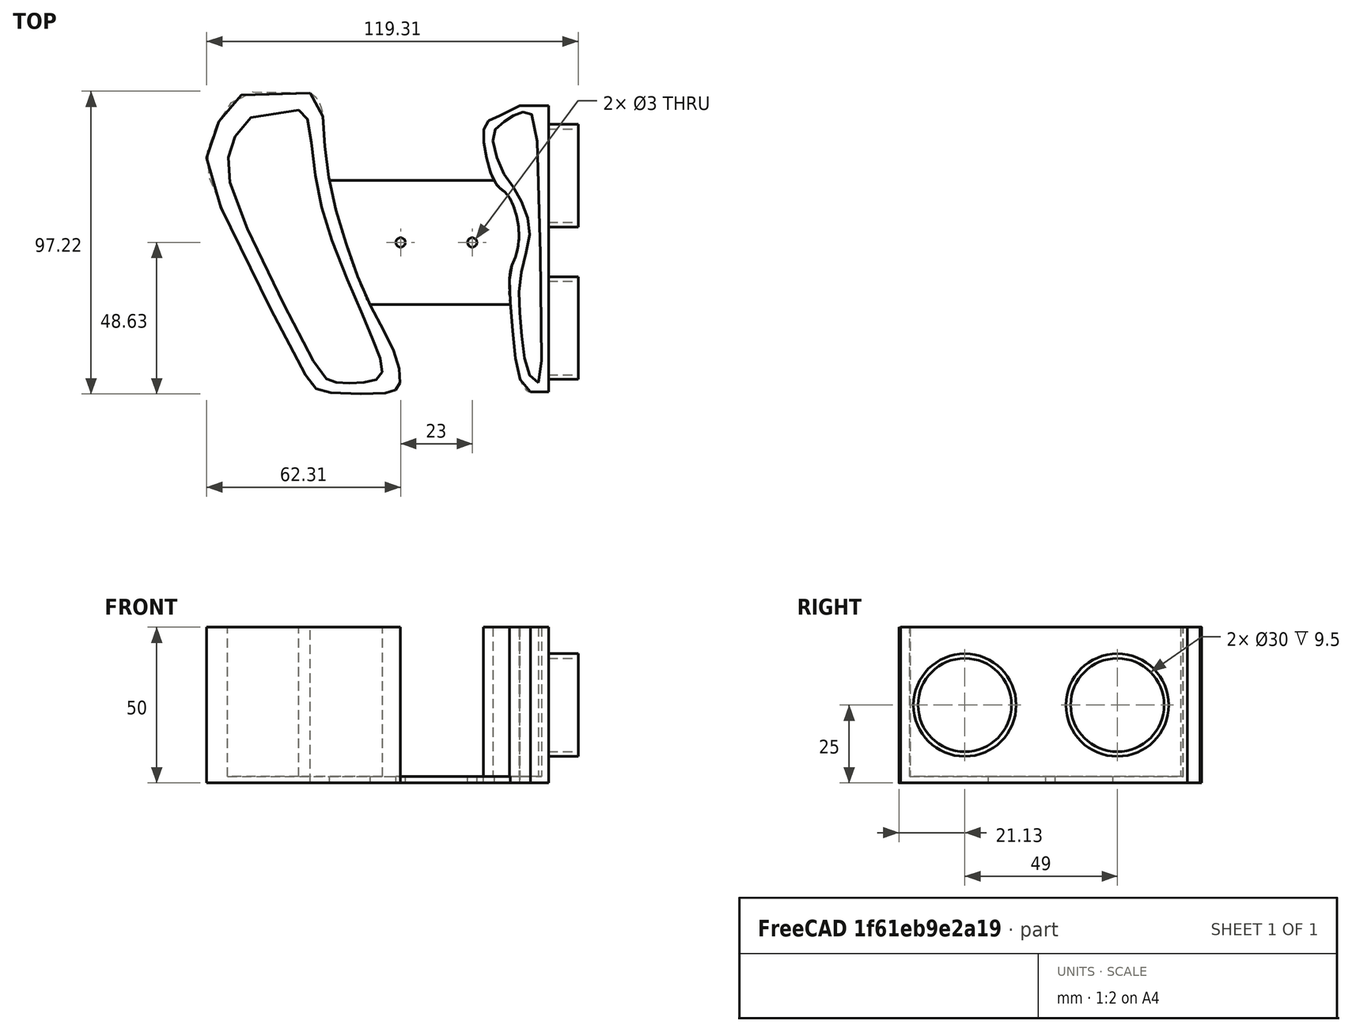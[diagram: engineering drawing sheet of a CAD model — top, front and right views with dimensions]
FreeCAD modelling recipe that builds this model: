
FCSTD DOCUMENT  (FreeCAD 0.18R4 (GitTag))
Label: soporte_pistola_calor
License: All rights reserved
LicenseURL: http://en.wikipedia.org/wiki/All_rights_reserved
objects: Sketcher::SketchObject×8, Part::Cut×6, Part::Cylinder×6, PartDesign::Pad×4, PartDesign::Body×4, Part::MultiFuse×4, Part::Box×3, Image::ImagePlane×1, PartDesign::ShapeBinder×1, App::DocumentObjectGroup×1, Mesh::Feature×1
note: 40 computed .brp shape members not serialized (recipe doc carries the construction recipe); baked Part::Feature solids carry a one-line shape summary decoded from their .brp

FEATURE [Image::ImagePlane] ImagePlane
  XSize = 218.296
  YSize = 300.157
FEATURE [Sketcher::SketchObject] Sketch
  MapMode = 5
  Support = -> [XY_Plane]
  sketch-geometry (39):
    g0-g19: Circle [constr] x20 (B-spline internal-alignment scaffolding for g20; pole/knot coordinates omitted)
    g20: BSplineCurve PolesCount=20 KnotsCount=18 Degree=3 IsPeriodic=0
    g21-g38: GeomPoint [constr] x18 (B-spline internal-alignment scaffolding for g20; pole/knot coordinates omitted)
  constraints (5):
    c: Radius(g0) = 0.7
    c: Equal(g0, g1-g19) x19
    c: Coincident(g19,g0)
    c: InternalAlignment(g0-g19 -> g20) x20
    c: InternalAlignment(g21-g38 -> g20) x18
FEATURE [PartDesign::Pad] Pad
  Length = 50
  Length2 = 100
  Profile = -> Sketch
  Refine = true
  Type = 0
FEATURE [PartDesign::Body] Body
  Group = -> [Sketch,Pad]
  Origin = -> Origin
  Tip = -> Pad
FEATURE [Sketcher::SketchObject] Sketch001
  MapMode = 5
  Support = -> [XY_Plane001]
  sketch-geometry (27):
    g0-g13: Circle [constr] x14 (B-spline internal-alignment scaffolding for g14; pole/knot coordinates omitted)
    g14: BSplineCurve PolesCount=14 KnotsCount=12 Degree=3 IsPeriodic=0
    g15-g26: GeomPoint [constr] x12 (B-spline internal-alignment scaffolding for g14; pole/knot coordinates omitted)
  constraints (5):
    c: Radius(g0) = 1
    c: Equal(g0, g1-g13) x13
    c: Coincident(g13,g0)
    c: InternalAlignment(g0-g13 -> g14) x14
    c: InternalAlignment(g15-g26 -> g14) x12
FEATURE [PartDesign::Pad] Pad001
  Length = 50
  Length2 = 100
  Profile = -> Sketch001
  Refine = true
  Type = 0
FEATURE [Part::Box] Box  label="Cube"
  AttacherType = Attacher::AttachEngine3D
  Height = 50
  Length = 6
  Placement = pos=(21.5,-33.57,0) rot=(0,0,1;0rad)
  Width = 90
FEATURE [Part::Box] Box001  label="Cube001"
  AttacherType = Attacher::AttachEngine3D
  Height = 50
  Length = 9.3
  Placement = pos=(18.2,0,0) rot=(0,0,1;0rad)
  Width = 58.5
FEATURE [Part::Box] Box002  label="Cube002"
  AttacherType = Attacher::AttachEngine3D
  Height = 2
  Length = 63
  Placement = pos=(-44,-5.5,0) rot=(0,0,1;0rad)
  Width = 40
FEATURE [Sketcher::SketchObject] Sketch002
  MapMode = 5
  Placement = pos=(0,0,50) rot=(0,0,1;0rad)
  Support = -> [Pad]
FEATURE [PartDesign::ShapeBinder] CopyPad
  Placement = pos=(0,0,50) rot=(0,0,1;0rad)
  TraceSupport = false
FEATURE [Sketcher::SketchObject] Sketch003
  MapMode = 5
  Placement = pos=(0,0,50) rot=(0,0,1;0rad)
  Support = -> [CopyPad]
  sketch-geometry (15):
    g0: Circle [constr] CenterX=-68.4142 CenterY=53.8043 CenterZ=0 NormalX=0 NormalY=0 NormalZ=1 AngleXU=0 Radius=1
    g1: Circle [constr] CenterX=-72.7746 CenterY=48.5095 CenterZ=0 NormalX=0 NormalY=0 NormalZ=1 AngleXU=0 Radius=1
    g2: Circle [constr] CenterX=-75.422 CenterY=38.8543 CenterZ=0 NormalX=0 NormalY=0 NormalZ=1 AngleXU=0 Radius=1
    g3: Circle [constr] CenterX=-69.0371 CenterY=19.0767 CenterZ=0 NormalX=0 NormalY=0 NormalZ=1 AngleXU=0 Radius=1
    g4: Circle [constr] CenterX=-52.6855 CenterY=-15.3396 CenterZ=0 NormalX=0 NormalY=0 NormalZ=1 AngleXU=0 Radius=1
    g5: Circle [constr] CenterX=-43.3418 CenterY=-29.0437 CenterZ=0 NormalX=0 NormalY=0 NormalZ=1 AngleXU=0 Radius=1
    g6: Circle [constr] CenterX=-26.2115 CenterY=-31.224 CenterZ=0 NormalX=0 NormalY=0 NormalZ=1 AngleXU=0 Radius=1
    g7: Circle [constr] CenterX=-24.187 CenterY=-25.9292 CenterZ=0 NormalX=0 NormalY=0 NormalZ=1 AngleXU=0 Radius=1
    g8: Circle [constr] CenterX=-27.1459 CenterY=-17.364 CenterZ=0 NormalX=0 NormalY=0 NormalZ=1 AngleXU=0 Radius=1
    g9: Circle [constr] CenterX=-38.047 CenterY=4.12663 CenterZ=0 NormalX=0 NormalY=0 NormalZ=1 AngleXU=0 Radius=1
    g10: Circle [constr] CenterX=-46.4564 CenterY=27.6418 CenterZ=0 NormalX=0 NormalY=0 NormalZ=1 AngleXU=0 Radius=1
    g11: Circle [constr] CenterX=-49.571 CenterY=47.2637 CenterZ=0 NormalX=0 NormalY=0 NormalZ=1 AngleXU=0 Radius=1
    g12: Circle [constr] CenterX=-50.3496 CenterY=56.6075 CenterZ=0 NormalX=0 NormalY=0 NormalZ=1 AngleXU=0 Radius=1
    g13: Circle [constr] CenterX=-62.9637 CenterY=58.6319 CenterZ=0 NormalX=0 NormalY=0 NormalZ=1 AngleXU=0 Radius=1
    g14: Circle [constr] CenterX=-70.1272 CenterY=57.3861 CenterZ=0 NormalX=0 NormalY=0 NormalZ=1 AngleXU=0 Radius=1
  constraints (2):
    c: Radius(g0) = 1
    c: Equal(g0, g1-g14) x14
FEATURE [PartDesign::Body] Body001
  Group = -> [Sketch001,Pad001,Sketch002,CopyPad,Sketch003]
  Origin = -> Origin001
  Tip = -> Pad001
FEATURE [Part::MultiFuse] Fusion
  Refine = true
  Shapes = -> [Body001,Box]
FEATURE [Part::MultiFuse] Fusion001
  Refine = true
  Shapes = -> [Box001,Fusion]
FEATURE [Sketcher::SketchObject] Sketch004
  MapMode = 5
  Placement = pos=(0,0,50) rot=(0,0,1;0rad)
  Support = -> [Pad]
  sketch-geometry (33):
    g0-g16: Circle [constr] x17 (B-spline internal-alignment scaffolding for g17; pole/knot coordinates omitted)
    g17: BSplineCurve PolesCount=17 KnotsCount=15 Degree=3 IsPeriodic=0
    g18-g32: GeomPoint [constr] x15 (B-spline internal-alignment scaffolding for g17; pole/knot coordinates omitted)
  constraints (5):
    c: Radius(g0) = 2
    c: Equal(g0, g1-g16) x16
    c: Coincident(g16,g0)
    c: InternalAlignment(g0-g16 -> g17) x17
    c: InternalAlignment(g18-g32 -> g17) x15
FEATURE [Sketcher::SketchObject] CopySketch004
  Placement = pos=(0,0,50) rot=(0,0,1;0rad)
  sketch-geometry (33):
    g0-g16: Circle [constr] x17 (B-spline internal-alignment scaffolding for g17; pole/knot coordinates omitted)
    g17: BSplineCurve PolesCount=17 KnotsCount=15 Degree=3 IsPeriodic=0
    g18-g32: GeomPoint [constr] x15 (B-spline internal-alignment scaffolding for g17; pole/knot coordinates omitted)
  constraints (5):
    c: Radius(g0) = 2
    c: Equal(g0, g1-g16) x16
    c: Coincident(g16,g0)
    c: InternalAlignment(g0-g16 -> g17) x17
    c: InternalAlignment(g18-g32 -> g17) x15
FEATURE [PartDesign::Pad] Pad002
  Length = 48
  Length2 = 100
  Placement = pos=(0,0,50) rot=(0,0,1;0rad)
  Profile = -> CopySketch004
  Refine = true
  Type = 0
FEATURE [PartDesign::Body] Body002
  Group = -> [Pad002]
  Origin = -> Origin002
  Placement = pos=(0,0,-48) rot=(0,0,1;0rad)
  Tip = -> Pad002
FEATURE [Part::Cut] Cut
  Base = -> Body
  Refine = true
  Tool = -> Body002
FEATURE [Sketcher::SketchObject] Sketch005
  MapMode = 5
  Placement = pos=(0,0,0) rot=(1,0,0;3.14159rad)
  Support = -> [Fusion001]
  sketch-geometry (39):
    g0-g19: Circle [constr] x20 (B-spline internal-alignment scaffolding for g20; pole/knot coordinates omitted)
    g20: BSplineCurve PolesCount=20 KnotsCount=18 Degree=3 IsPeriodic=0
    g21-g38: GeomPoint [constr] x18 (B-spline internal-alignment scaffolding for g20; pole/knot coordinates omitted)
  constraints (5):
    c: Radius(g0) = 0.2
    c: Equal(g0, g1-g19) x19
    c: Coincident(g19,g0)
    c: InternalAlignment(g0-g19 -> g20) x20
    c: InternalAlignment(g21-g38 -> g20) x18
FEATURE [App::DocumentObjectGroup] Group
  Group = -> [Sketch004,Sketch005]
FEATURE [Sketcher::SketchObject] CopySketch005
  Placement = pos=(0,0,0) rot=(1,0,0;3.14159rad)
  sketch-geometry (39):
    g0-g19: Circle [constr] x20 (B-spline internal-alignment scaffolding for g20; pole/knot coordinates omitted)
    g20: BSplineCurve PolesCount=20 KnotsCount=18 Degree=3 IsPeriodic=0
    g21-g38: GeomPoint [constr] x18 (B-spline internal-alignment scaffolding for g20; pole/knot coordinates omitted)
  constraints (5):
    c: Radius(g0) = 0.2
    c: Equal(g0, g1-g19) x19
    c: Coincident(g19,g0)
    c: InternalAlignment(g0-g19 -> g20) x20
    c: InternalAlignment(g21-g38 -> g20) x18
FEATURE [PartDesign::Pad] Pad003
  Length = 48
  Length2 = 100
  Placement = pos=(0,0,0) rot=(1,0,0;3.14159rad)
  Profile = -> CopySketch005
  Refine = true
  Type = 0
FEATURE [PartDesign::Body] Body003
  Group = -> [Pad003]
  Origin = -> Origin003
  Placement = pos=(0,0,50) rot=(0,0,1;0rad)
  Tip = -> Pad003
FEATURE [Part::Cut] Cut001
  Base = -> Fusion001
  Refine = true
  Tool = -> Body003
FEATURE [Part::MultiFuse] Fusion002
  Refine = true
  Shapes = -> [Box002,Cut,Cut001]
FEATURE [Part::Cylinder] Cylinder
  Angle = 360
  AttacherType = Attacher::AttachEngine3D
  Height = 10
  Placement = pos=(3,14.5,-4) rot=(0,0,1;0rad)
  Radius = 1.5
FEATURE [Part::Cylinder] Cylinder001
  Angle = 360
  AttacherType = Attacher::AttachEngine3D
  Height = 10
  Placement = pos=(-20,14.5,-4) rot=(0,0,1;0rad)
  Radius = 1.5
FEATURE [Part::Cut] Cut002
  Base = -> Fusion002
  Refine = true
  Tool = -> Cylinder
FEATURE [Part::Cut] Cut003
  Base = -> Cut002
  Refine = true
  Tool = -> Cylinder001
FEATURE [Part::Cylinder] Cylinder002
  Angle = 360
  AttacherType = Attacher::AttachEngine3D
  Height = 10
  Placement = pos=(27,-13,25) rot=(0,1,0;1.5708rad)
  Radius = 16.5
FEATURE [Part::Cylinder] Cylinder003
  Angle = 360
  AttacherType = Attacher::AttachEngine3D
  Height = 10
  Placement = pos=(27,36,25) rot=(0,1,0;1.5708rad)
  Radius = 16.5
FEATURE [Part::Cylinder] Cylinder004
  Angle = 360
  AttacherType = Attacher::AttachEngine3D
  Height = 10
  Placement = pos=(27,-13,25) rot=(0,1,0;1.5708rad)
  Radius = 15
FEATURE [Part::Cylinder] Cylinder005
  Angle = 360
  AttacherType = Attacher::AttachEngine3D
  Height = 10
  Placement = pos=(27,36,25) rot=(0,1,0;1.5708rad)
  Radius = 15
FEATURE [Part::Cut] Cut004
  Base = -> Cylinder002
  Refine = true
  Tool = -> Cylinder004
FEATURE [Part::Cut] Cut005
  Base = -> Cylinder003
  Refine = true
  Tool = -> Cylinder005
FEATURE [Part::MultiFuse] Fusion003
  Refine = true
  Shapes = -> [Cut003,Cut005,Cut004]
FEATURE [Mesh::Feature] Mesh  label="Fusion003 (Meshed)"
